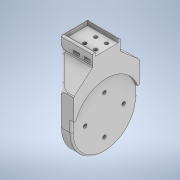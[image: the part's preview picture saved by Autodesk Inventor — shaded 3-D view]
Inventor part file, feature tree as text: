
AUTODESK INVENTOR PART (.ipt)
format: ipt  version: 2022 (Build 260153000, 153)  size: 545,280 bytes
history: native  units: mm
features: sketch x12, extrude x11, other x6, projected_geometry x4, chamfer x2, loft x1, fillet x1
ambient origin geometry x8: Origin, YZ Plane, XZ Plane, XY Plane, X Axis, Y Axis, Z Axis, Center Point
bodies: Body1 (feature_tree)
feature tree (37):
  other  "Твердое тело1"
  extrude  "Выдавливание1"  Depth=20.0mm
  extrude  "Выдавливание2"  Depth=55.6mm
  extrude  "Выдавливание4"  Depth=2.5mm
  extrude  "Выдавливание9"  Depth=2.0mm
  other  "РабПлоскость2"
  extrude  "Выдавливание10"  Depth=2.0mm TaperAngle=0.0deg
  extrude  "Выдавливание11"  Depth=2.0mm
  other  "РабПлоскость3"
  loft  "Лофт1"
  other  "РабПлоскость5"
  sketch  "Эскиз18"
  other  "РабПлоскость6"
  extrude  "Выдавливание14"  Depth=5.0mm TaperAngle=0.0deg
  extrude  "Выдавливание15"  Depth=14.0mm
  other  "РабПлоскость7"
  sketch  "Эскиз20"
  chamfer  "Фаска1"  Distance=40.0mm Angle=360.0deg
  extrude  "Выдавливание17"  Depth=3.2mm
  extrude  "Выдавливание18"  Depth=6.2mm
  chamfer  "Фаска2"  Distance=14.0mm
  fillet  "Сопряжение6"  [1 undecoded]
  extrude  "Выдавливание19"  Depth=9.9mm
  sketch  "Эскиз1"
  sketch  "Эскиз2"
  projected_geometry  "Спроецированная петля1"
  sketch  "Эскиз12"
  projected_geometry  "Спроецированная петля4"
  sketch  "Эскиз13"
  sketch  "Эскиз14"
  projected_geometry  "Спроецированная петля5"
  sketch  "Эскиз15"
  sketch  "Эскиз17"
  sketch  "Эскиз19"
  sketch  "Эскиз21"
  projected_geometry  "Спроецированная петля6"
  sketch  "Эскиз22"
note: 1 required parameter value undecoded (feature->parameter linkage not recoverable at this tier; creation-order binding heuristic only, values carry confidence <= 0.55)
